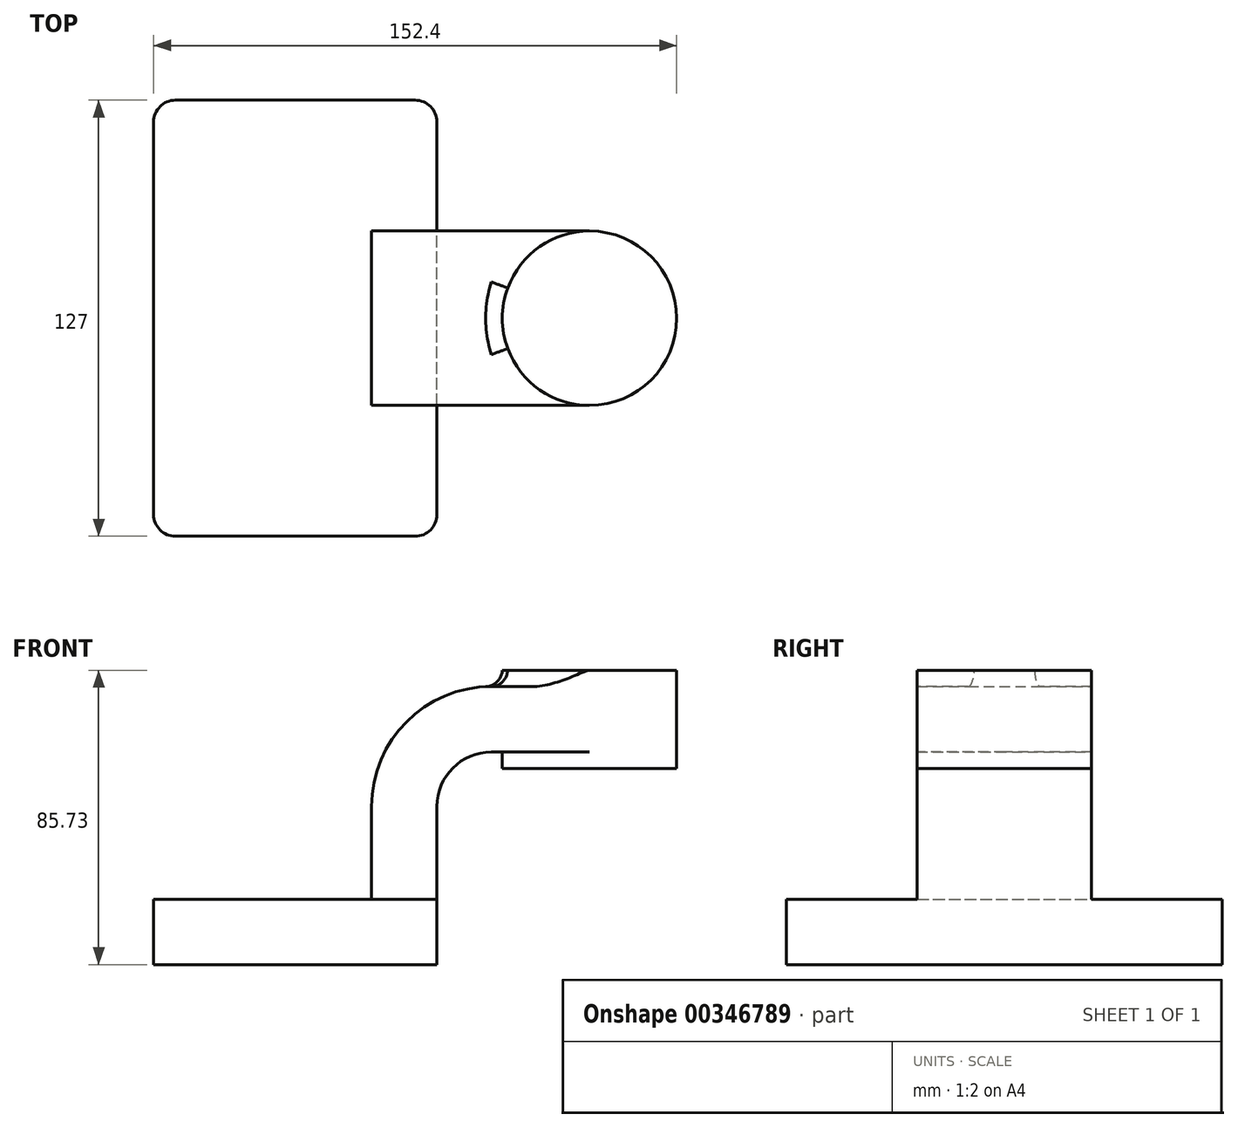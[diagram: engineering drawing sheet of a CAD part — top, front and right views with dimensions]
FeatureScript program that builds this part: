
annotation { "Feature Type Name" : "Feature", "Feature Type Description" : "" }
export const myFeature = defineFeature(function(context is Context, id is Id, definition is map)
    precondition{}
    {
        {
            var Q0;
            Q0=qCreatedBy(makeId("Front.planeOp"),FACE);
            var sketch = newSketch(context, id + "F0", { "sketchPlane" : qUnion([Q0])});
            skLineSegment(sketch, "E0.bottom", {"start": v(41.27, 9.53) * mm, "end": v(-41.28, 9.53) * mm});
            skLineSegment(sketch, "E0.top", {"start": v(41.28, -9.52) * mm, "end": v(-41.27, -9.52) * mm});
            skLineSegment(sketch, "E0.left", {"start": v(41.28, 9.53) * mm, "end": v(41.28, -9.52) * mm});
            skLineSegment(sketch, "E0.right", {"start": v(-41.28, 9.53) * mm, "end": v(-41.27, -9.52) * mm});
            skPoint(sketch, "E0.middle", {"position": v(0, 0) * mm});
            skLineSegment(sketch, "E1.bottom", {"start": v(111.12, 47.63) * mm, "end": v(60.32, 47.63) * mm});
            skLineSegment(sketch, "E1.top", {"start": v(111.12, 76.2) * mm, "end": v(60.32, 76.2) * mm});
            skLineSegment(sketch, "E1.left", {"start": v(111.12, 47.63) * mm, "end": v(111.12, 76.2) * mm});
            skLineSegment(sketch, "E1.right", {"start": v(60.32, 47.63) * mm, "end": v(60.32, 76.2) * mm});
            skPoint(sketch, "E1.middle", {"position": v(85.72, 61.91) * mm});
            skLineSegment(sketch, "E2", {"start": v(41.27, 9.53) * mm, "end": v(41.27, 36.51) * mm});
            skArc(sketch, "E3", {"start": v(41.27, 36.51) * mm, "mid": v(45.92, 47.74) * mm, "end": v(57.15, 52.39) * mm});
            skLineSegment(sketch, "E4", {"start": v(57.15, 52.39) * mm, "end": v(85.72, 52.39) * mm});
            skLineSegment(sketch, "E5.0", {"start": v(57.15, 71.44) * mm, "end": v(85.72, 71.44) * mm});
            skArc(sketch, "E5.1", {"start": v(22.22, 36.51) * mm, "mid": v(32.45, 61.2) * mm, "end": v(57.15, 71.44) * mm});
            skLineSegment(sketch, "E5.2", {"start": v(22.22, 9.53) * mm, "end": v(22.22, 36.51) * mm});
            skLineSegment(sketch, "E6", {"start": v(85.72, 47.63) * mm, "end": v(85.72, 76.2) * mm});
            skFitSpline(sketch, "E7", {"points": [v(-41.28, 9.53) * mm, v(57.15, 71.44) * mm], "startDerivative": vector(139.58, 36.09) * mm, "endDerivative": vector(174.28, -0.23) * mm});
            skSolve(sketch);
        }
        {
            var Q0;
            Q0=makeQuery(id+"F0.imprint","IMPRINT",FACE,{"disambiguationData":[TD([[makeQuery(id+"F0.imprint","IMPRINT",EDGE,{"derivedFrom":sQuery(id+"F0.wireOp",EDGE,"E0.top")}),-1.0]])]});
            extrude(context, id + "F1", {"entities" : qUnion([Q0]), "endBound" : BoundingType.SYMMETRIC, "depth" : 127 * mm});
        }
        {
            var Q0;
            {var subQ1=sQuery(id+"F0.wireOp",EDGE,"E2");Q0=makeQuery(id+"F0.imprint","IMPRINT",FACE,{"disambiguationData":[TD([[makeQuery(id+"F0.imprint","IMPRINT",EDGE,{"derivedFrom":subQ1}),1.0]])]});}
            var Q1;
            {var subQ0=sQuery(id+"F0.wireOp",EDGE,"E4");var subQ1=sQuery(id+"F0.wireOp",EDGE,"E1.right");var subQ2=makeQuery(id+"F0.imprint","INTERSECT",VERTEX,{"derivedFrom":[subQ1,subQ0]});Q1=makeQuery(id+"F0.imprint","IMPRINT",FACE,{"disambiguationData":[TD([[makeQuery(id+"F0.imprint","IMPRINT",EDGE,{"disambiguationData":[TD([[subQ2,-1.0]])],"derivedFrom":subQ1}),-1.0]])]});}
            extrude(context, id + "F2", {"entities" : qUnion([Q0, Q1]), "operationType" : NewBodyOperationType.ADD, "endBound" : BoundingType.SYMMETRIC, "depth" : 50.8 * mm});
        }
        {
            var Q0;
            Q0=makeQuery(id+"F0.imprint","IMPRINT",FACE,{"disambiguationData":[TD([[makeQuery(id+"F0.imprint","IMPRINT",EDGE,{"derivedFrom":sQuery(id+"F0.wireOp",EDGE,"E5.1")}),1.0]])]});
            extrude(context, id + "F3", {"entities" : qUnion([Q0]), "operationType" : NewBodyOperationType.ADD, "endBound" : BoundingType.SYMMETRIC, "depth" : 15.88 * mm});
        }
        {
            var Q0;
            {var subQ4=sQuery(id+"F0.wireOp",EDGE,"E1.left");Q0=makeQuery(id+"F0.imprint","IMPRINT",FACE,{"disambiguationData":[TD([[makeQuery(id+"F0.imprint","IMPRINT",EDGE,{"derivedFrom":subQ4}),1.0]])]});}
            var Q1;
            Q1=sQuery(id+"F0.wireOp",EDGE,"E6");
            revolve(context, id + "F4", {"operationType" : NewBodyOperationType.ADD, "entities" : qUnion([Q0]), "axis" : qUnion([Q1]), "revolveType" : RevolveType.FULL});
        }
        {
            var Q0;
            Q0=makeQuery(id+"F1.opExtrude","CAP_EDGE",EDGE,{"disambiguationData":[OSD([sQuery(id+"F0.wireOp",EDGE,"E0.left")])],"isStart":true});
            var Q1;
            Q1=makeQuery(id+"F1.opExtrude","CAP_EDGE",EDGE,{"disambiguationData":[OSD([sQuery(id+"F0.wireOp",EDGE,"E0.right")])],"isStart":true});
            var Q2;
            Q2=makeQuery(id+"F1.opExtrude","CAP_EDGE",EDGE,{"disambiguationData":[OSD([sQuery(id+"F0.wireOp",EDGE,"E0.left")])],"isStart":false});
            var Q3;
            Q3=makeQuery(id+"F1.opExtrude","CAP_EDGE",EDGE,{"disambiguationData":[OSD([sQuery(id+"F0.wireOp",EDGE,"E0.right")])],"isStart":false});
            fillet(context, id + "F5", {"entities" : qUnion([Q0, Q1, Q2, Q3]), "radius" : 6.35 * mm, "tangentPropagation" : true, "allowEdgeOverflow" : false});
        }
        {
            var Q0;
            Q0=makeQuery(id+"F4.boolean.opBoolean","INTERSECT",EDGE,{"derivedFrom":[makeQuery(id+"F2.opExtrude","SWEPT_FACE",FACE,{"disambiguationData":[OSD([sQuery(id+"F0.wireOp",EDGE,"E5.0")])]}),makeQuery(id+"F4.opRevolve","SWEPT_FACE",FACE,{"disambiguationData":[OSD([sQuery(id+"F0.wireOp",EDGE,"E1.left")])]})]});
            fillet(context, id + "F6", {"entities" : qUnion([Q0]), "radius" : 5.08 * mm, "tangentPropagation" : true, "allowEdgeOverflow" : false});
        }
    });
